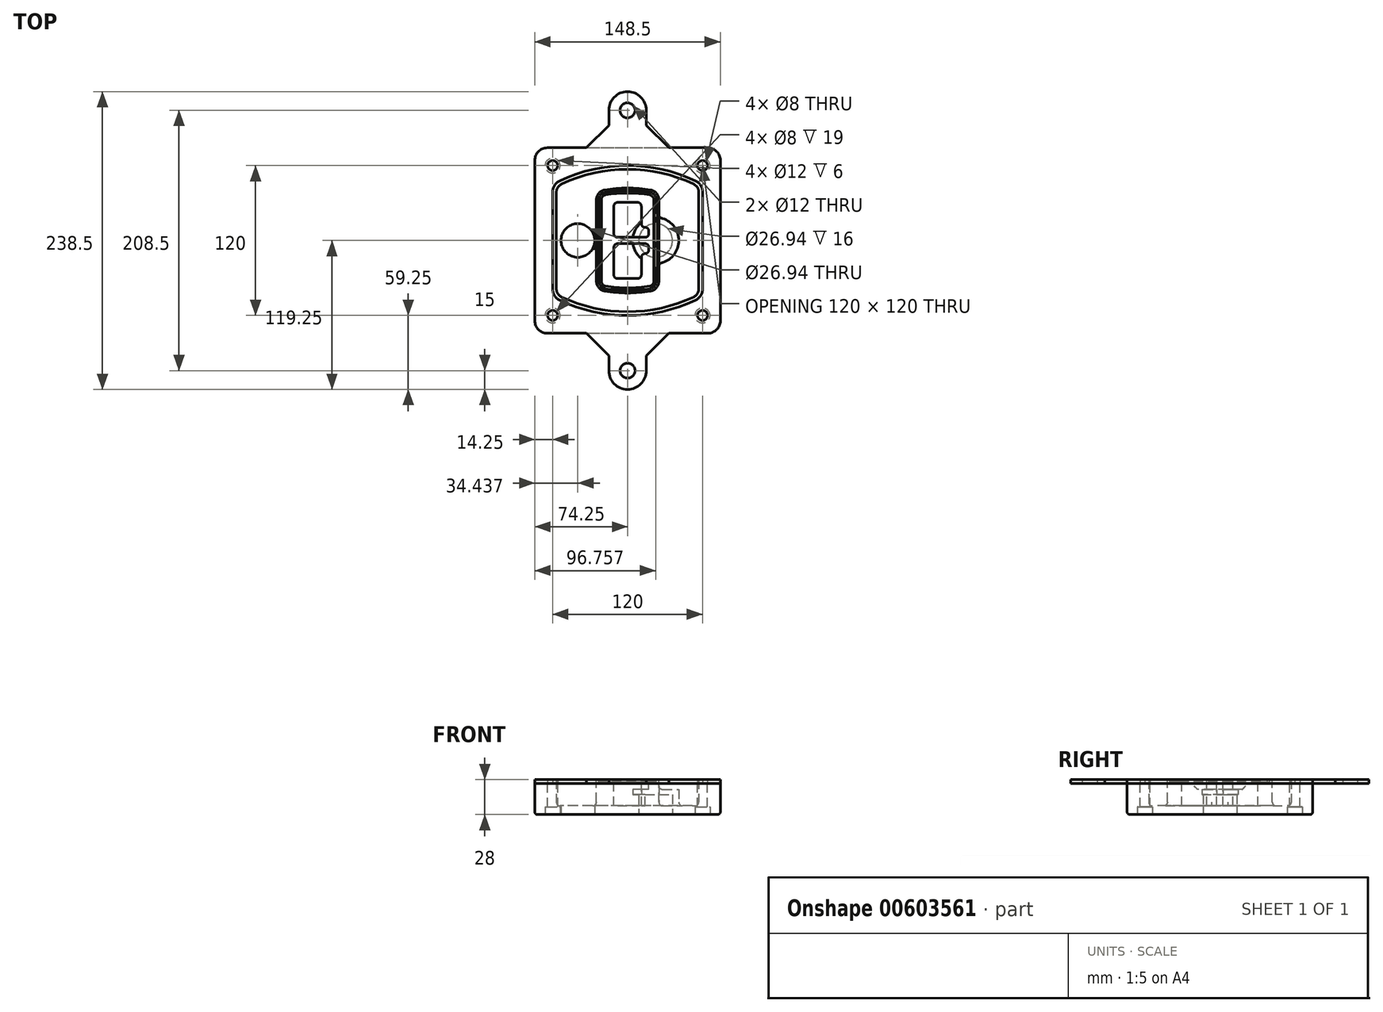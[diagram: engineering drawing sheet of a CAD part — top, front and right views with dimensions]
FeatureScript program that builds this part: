
annotation { "Feature Type Name" : "Feature", "Feature Type Description" : "" }
export const myFeature = defineFeature(function(context is Context, id is Id, definition is map)
    precondition{}
    {
        {
            var Q0;
            Q0=qCreatedBy(makeId("Top.planeOp"),FACE);
            var sketch = newSketch(context, id + "F0", { "sketchPlane" : qUnion([Q0])});
            skPoint(sketch, "E0.rect.middle", {"position": v(0, 0) * mm});
            skLineSegment(sketch, "E1.bottom", {"start": v(-64.25, -74.25) * mm, "end": v(64.25, -74.25) * mm});
            skLineSegment(sketch, "E1.top", {"start": v(-64.25, 74.25) * mm, "end": v(64.25, 74.25) * mm});
            skLineSegment(sketch, "E1.left", {"start": v(-74.25, -64.25) * mm, "end": v(-74.25, 64.25) * mm});
            skLineSegment(sketch, "E1.right", {"start": v(74.25, -64.25) * mm, "end": v(74.25, 64.25) * mm});
            skLineSegment(sketch, "E2", {"start": v(-74.25, 74.25) * mm, "end": v(74.25, -74.25) * mm, "construction": true});
            skLineSegment(sketch, "E3", {"start": v(74.25, 74.25) * mm, "end": v(-74.25, -74.25) * mm, "construction": true});
            skCircle(sketch, "E4", {"center": v(-60, 60) * mm, "radius": 4 * mm});
            skCircle(sketch, "E5", {"center": v(60, 60) * mm, "radius": 4 * mm});
            skCircle(sketch, "E6", {"center": v(60, -60) * mm, "radius": 4 * mm});
            skCircle(sketch, "E7", {"center": v(-60, -60) * mm, "radius": 4 * mm});
            skLineSegment(sketch, "E8", {"start": v(-60, 60) * mm, "end": v(60, 60) * mm, "construction": true});
            skLineSegment(sketch, "E9", {"start": v(60, 60) * mm, "end": v(60, -60) * mm, "construction": true});
            skLineSegment(sketch, "E10", {"start": v(60, -60) * mm, "end": v(-60, -60) * mm, "construction": true});
            skLineSegment(sketch, "E11", {"start": v(-60, -60) * mm, "end": v(-60, 60) * mm, "construction": true});
            skLineSegment(sketch, "E12", {"start": v(-60, 38.83) * mm, "end": v(-60, -38.83) * mm});
            skLineSegment(sketch, "E13", {"start": v(60, 38.83) * mm, "end": v(60, -38.83) * mm});
            skArc(sketch, "E14", {"start": v(54.26, 47.88) * mm, "mid": v(0, 60) * mm, "end": v(-54.26, 47.88) * mm});
            skArc(sketch, "E15", {"start": v(-54.26, -47.88) * mm, "mid": v(0, -60) * mm, "end": v(54.26, -47.88) * mm});
            skLineSegment(sketch, "E16", {"start": v(-60, 0) * mm, "end": v(60, 0) * mm, "construction": true});
            skPoint(sketch, "E17.visualSharp", {"position": v(-60, -45) * mm});
            skArc(sketch, "E17.filletArc", {"start": v(-60, -38.83) * mm, "mid": v(-58.44, -44.2) * mm, "end": v(-54.26, -47.88) * mm});
            skPoint(sketch, "E18.visualSharp", {"position": v(-60, 45) * mm});
            skArc(sketch, "E18.filletArc", {"start": v(-54.26, 47.88) * mm, "mid": v(-58.44, 44.2) * mm, "end": v(-60, 38.83) * mm});
            skPoint(sketch, "E19.visualSharp", {"position": v(60, 45) * mm});
            skArc(sketch, "E19.filletArc", {"start": v(60, 38.83) * mm, "mid": v(58.44, 44.2) * mm, "end": v(54.26, 47.88) * mm});
            skPoint(sketch, "E20.visualSharp", {"position": v(60, -45) * mm});
            skArc(sketch, "E20.filletArc", {"start": v(54.26, -47.88) * mm, "mid": v(58.44, -44.2) * mm, "end": v(60, -38.83) * mm});
            skPoint(sketch, "E21.visualSharp", {"position": v(-74.25, 74.25) * mm});
            skArc(sketch, "E21.filletArc", {"start": v(-64.25, 74.25) * mm, "mid": v(-71.32, 71.32) * mm, "end": v(-74.25, 64.25) * mm});
            skPoint(sketch, "E22.visualSharp", {"position": v(74.25, 74.25) * mm});
            skArc(sketch, "E22.filletArc", {"start": v(74.25, 64.25) * mm, "mid": v(71.32, 71.32) * mm, "end": v(64.25, 74.25) * mm});
            skPoint(sketch, "E23.visualSharp", {"position": v(74.25, -74.25) * mm});
            skArc(sketch, "E23.filletArc", {"start": v(64.25, -74.25) * mm, "mid": v(71.32, -71.32) * mm, "end": v(74.25, -64.25) * mm});
            skPoint(sketch, "E24.visualSharp", {"position": v(-74.25, -74.25) * mm});
            skArc(sketch, "E24.filletArc", {"start": v(-74.25, -64.25) * mm, "mid": v(-71.32, -71.32) * mm, "end": v(-64.25, -74.25) * mm});
            skArc(sketch, "E25.0", {"start": v(57, 38.83) * mm, "mid": v(55.9, 42.58) * mm, "end": v(52.98, 45.17) * mm});
            skLineSegment(sketch, "E25.1", {"start": v(57, 38.83) * mm, "end": v(57, -38.83) * mm});
            skArc(sketch, "E25.2", {"start": v(52.98, -45.17) * mm, "mid": v(55.9, -42.58) * mm, "end": v(57, -38.83) * mm});
            skArc(sketch, "E25.3", {"start": v(-52.98, -45.17) * mm, "mid": v(0, -57) * mm, "end": v(52.98, -45.17) * mm});
            skArc(sketch, "E25.4", {"start": v(-57, -38.83) * mm, "mid": v(-55.9, -42.58) * mm, "end": v(-52.98, -45.17) * mm});
            skArc(sketch, "E25.5", {"start": v(52.98, 45.17) * mm, "mid": v(0, 57) * mm, "end": v(-52.98, 45.17) * mm});
            skLineSegment(sketch, "E25.6", {"start": v(-57, 38.83) * mm, "end": v(-57, -38.83) * mm});
            skArc(sketch, "E25.7", {"start": v(-52.98, 45.17) * mm, "mid": v(-55.9, 42.58) * mm, "end": v(-57, 38.83) * mm});
            skArc(sketch, "E26.0", {"start": v(-55.96, 51.5) * mm, "mid": v(-61.82, 46.33) * mm, "end": v(-64, 38.83) * mm});
            skArc(sketch, "E26.1", {"start": v(55.96, 51.5) * mm, "mid": v(0, 64) * mm, "end": v(-55.96, 51.5) * mm});
            skArc(sketch, "E26.2", {"start": v(64, 38.83) * mm, "mid": v(61.82, 46.33) * mm, "end": v(55.96, 51.5) * mm});
            skLineSegment(sketch, "E26.3", {"start": v(64, 38.83) * mm, "end": v(64, -38.83) * mm});
            skArc(sketch, "E26.4", {"start": v(55.96, -51.5) * mm, "mid": v(61.82, -46.33) * mm, "end": v(64, -38.83) * mm});
            skLineSegment(sketch, "E26.5", {"start": v(-64, 38.83) * mm, "end": v(-64, -38.83) * mm});
            skArc(sketch, "E26.6", {"start": v(-55.96, -51.5) * mm, "mid": v(0, -64) * mm, "end": v(55.96, -51.5) * mm});
            skArc(sketch, "E26.7", {"start": v(-64, -38.83) * mm, "mid": v(-61.82, -46.33) * mm, "end": v(-55.96, -51.5) * mm});
            skSolve(sketch);
        }
        {
            var Q0;
            Q0=makeQuery(id+"F0.imprint","IMPRINT",FACE,{"disambiguationData":[TD([[makeQuery(id+"F0.imprint","IMPRINT",EDGE,{"derivedFrom":sQuery(id+"F0.wireOp",EDGE,"E1.bottom")}),1.0]])]});
            var Q1;
            Q1=makeQuery(id+"F0.imprint","IMPRINT",FACE,{"disambiguationData":[TD([[makeQuery(id+"F0.imprint","IMPRINT",EDGE,{"derivedFrom":sQuery(id+"F0.wireOp",EDGE,"E12")}),1.0]])]});
            var Q2;
            Q2=makeQuery(id+"F0.imprint","IMPRINT",FACE,{"disambiguationData":[TD([[makeQuery(id+"F0.imprint","IMPRINT",EDGE,{"derivedFrom":sQuery(id+"F0.wireOp",EDGE,"E25.0")}),1.0]])]});
            var Q3;
            Q3=makeQuery(id+"F0.imprint","IMPRINT",FACE,{"disambiguationData":[TD([[makeQuery(id+"F0.imprint","IMPRINT",EDGE,{"derivedFrom":sQuery(id+"F0.wireOp",EDGE,"E12")}),-1.0]])]});
            extrude(context, id + "F1", {"entities" : qUnion([Q0, Q1, Q2, Q3]), "oppositeDirection" : true, "depth" : 25 * mm});
        }
        {
            var Q0;
            Q0=makeQuery(id+"F0.imprint","IMPRINT",FACE,{"disambiguationData":[TD([[makeQuery(id+"F0.imprint","IMPRINT",EDGE,{"derivedFrom":sQuery(id+"F0.wireOp",EDGE,"E12")}),1.0]])]});
            extrude(context, id + "F2", {"entities" : qUnion([Q0]), "operationType" : NewBodyOperationType.ADD, "depth" : 3 * mm});
        }
        {
            var Q0;
            Q0=makeQuery(id+"F0.imprint","IMPRINT",FACE,{"disambiguationData":[TD([[makeQuery(id+"F0.imprint","IMPRINT",EDGE,{"derivedFrom":sQuery(id+"F0.wireOp",EDGE,"E25.0")}),1.0]])]});
            extrude(context, id + "F3", {"entities" : qUnion([Q0]), "operationType" : NewBodyOperationType.REMOVE, "oppositeDirection" : true, "depth" : 18 * mm});
        }
        {
            var Q0;
            Q0=makeQuery(id+"F2.opExtrude","CAP_FACE",FACE,{"disambiguationData":[OSD([sQuery(id+"F0.wireOp",EDGE,"E12"),sQuery(id+"F0.wireOp",EDGE,"E13"),sQuery(id+"F0.wireOp",EDGE,"E14"),sQuery(id+"F0.wireOp",EDGE,"E15"),sQuery(id+"F0.wireOp",EDGE,"E17.filletArc"),sQuery(id+"F0.wireOp",EDGE,"E18.filletArc"),sQuery(id+"F0.wireOp",EDGE,"E19.filletArc"),sQuery(id+"F0.wireOp",EDGE,"E20.filletArc"),sQuery(id+"F0.wireOp",EDGE,"E25.0"),sQuery(id+"F0.wireOp",EDGE,"E25.1"),sQuery(id+"F0.wireOp",EDGE,"E25.2"),sQuery(id+"F0.wireOp",EDGE,"E25.3"),sQuery(id+"F0.wireOp",EDGE,"E25.4"),sQuery(id+"F0.wireOp",EDGE,"E25.5"),sQuery(id+"F0.wireOp",EDGE,"E25.6"),sQuery(id+"F0.wireOp",EDGE,"E25.7")])],"isStart":false});
            var sketch = newSketch(context, id + "F4", { "sketchPlane" : qUnion([Q0])});
            skArc(sketch, "E27.0", {"start": v(-18.34, -40.45) * mm, "mid": v(0, -42) * mm, "end": v(18.34, -40.45) * mm});
            skArc(sketch, "E28.0", {"start": v(18.34, 40.45) * mm, "mid": v(0, 42) * mm, "end": v(-18.34, 40.45) * mm});
            skLineSegment(sketch, "E29", {"start": v(-25, 32.57) * mm, "end": v(-25, -32.57) * mm});
            skLineSegment(sketch, "E30", {"start": v(25, 32.57) * mm, "end": v(25, -32.57) * mm});
            skLineSegment(sketch, "E31", {"start": v(-25, 39.1) * mm, "end": v(25, 39.1) * mm, "construction": true});
            skLineSegment(sketch, "E32", {"start": v(-25, -39.1) * mm, "end": v(25, -39.1) * mm, "construction": true});
            skPoint(sketch, "E33.visualSharp", {"position": v(-25, 39.1) * mm});
            skArc(sketch, "E33.filletArc", {"start": v(-18.34, 40.45) * mm, "mid": v(-23.11, 37.73) * mm, "end": v(-25, 32.57) * mm});
            skPoint(sketch, "E34.visualSharp", {"position": v(25, 39.1) * mm});
            skArc(sketch, "E34.filletArc", {"start": v(25, 32.57) * mm, "mid": v(23.11, 37.73) * mm, "end": v(18.34, 40.45) * mm});
            skPoint(sketch, "E35.visualSharp", {"position": v(25, -39.1) * mm});
            skArc(sketch, "E35.filletArc", {"start": v(18.34, -40.45) * mm, "mid": v(23.11, -37.73) * mm, "end": v(25, -32.57) * mm});
            skPoint(sketch, "E36.visualSharp", {"position": v(-25, -39.1) * mm});
            skArc(sketch, "E36.filletArc", {"start": v(-25, -32.57) * mm, "mid": v(-23.11, -37.73) * mm, "end": v(-18.34, -40.45) * mm});
            skArc(sketch, "E37.0", {"start": v(52.98, 45.17) * mm, "mid": v(0, 57) * mm, "end": v(-52.98, 45.17) * mm});
            skArc(sketch, "E37.1", {"start": v(-52.98, 45.17) * mm, "mid": v(-55.9, 42.58) * mm, "end": v(-57, 38.83) * mm});
            skLineSegment(sketch, "E37.2", {"start": v(-57, 38.83) * mm, "end": v(-57, -38.83) * mm});
            skArc(sketch, "E37.3", {"start": v(-57, -38.83) * mm, "mid": v(-55.9, -42.58) * mm, "end": v(-52.98, -45.17) * mm});
            skArc(sketch, "E37.4", {"start": v(-52.98, -45.17) * mm, "mid": v(0, -57) * mm, "end": v(52.98, -45.17) * mm});
            skArc(sketch, "E37.5", {"start": v(52.98, -45.17) * mm, "mid": v(55.9, -42.58) * mm, "end": v(57, -38.83) * mm});
            skLineSegment(sketch, "E37.6", {"start": v(57, 38.83) * mm, "end": v(57, -38.83) * mm});
            skArc(sketch, "E37.7", {"start": v(57, 38.83) * mm, "mid": v(55.9, 42.58) * mm, "end": v(52.98, 45.17) * mm});
            skLineSegment(sketch, "E38.0", {"start": v(23, 32.57) * mm, "end": v(23, -32.57) * mm});
            skArc(sketch, "E38.1", {"start": v(18, -38.48) * mm, "mid": v(21.58, -36.44) * mm, "end": v(23, -32.57) * mm});
            skArc(sketch, "E38.2", {"start": v(-18, -38.48) * mm, "mid": v(0, -40) * mm, "end": v(18, -38.48) * mm});
            skArc(sketch, "E38.3", {"start": v(-23, -32.57) * mm, "mid": v(-21.58, -36.44) * mm, "end": v(-18, -38.48) * mm});
            skLineSegment(sketch, "E38.4", {"start": v(-23, 32.57) * mm, "end": v(-23, -32.57) * mm});
            skArc(sketch, "E38.5", {"start": v(23, 32.57) * mm, "mid": v(21.58, 36.44) * mm, "end": v(18, 38.48) * mm});
            skArc(sketch, "E38.6", {"start": v(-18, 38.48) * mm, "mid": v(-21.58, 36.44) * mm, "end": v(-23, 32.57) * mm});
            skArc(sketch, "E38.7", {"start": v(18, 38.48) * mm, "mid": v(0, 40) * mm, "end": v(-18, 38.48) * mm});
            skArc(sketch, "E39.0", {"start": v(21, 32.57) * mm, "mid": v(20.06, 35.15) * mm, "end": v(17.67, 36.5) * mm});
            skLineSegment(sketch, "E39.1", {"start": v(21, 32.57) * mm, "end": v(21, -32.57) * mm});
            skArc(sketch, "E39.2", {"start": v(17.67, -36.5) * mm, "mid": v(20.06, -35.15) * mm, "end": v(21, -32.57) * mm});
            skArc(sketch, "E39.3", {"start": v(-17.67, -36.5) * mm, "mid": v(0, -38) * mm, "end": v(17.67, -36.5) * mm});
            skArc(sketch, "E39.4", {"start": v(-21, -32.57) * mm, "mid": v(-20.06, -35.15) * mm, "end": v(-17.67, -36.5) * mm});
            skArc(sketch, "E39.5", {"start": v(17.67, 36.5) * mm, "mid": v(0, 38) * mm, "end": v(-17.67, 36.5) * mm});
            skLineSegment(sketch, "E39.6", {"start": v(-21, 32.57) * mm, "end": v(-21, -32.57) * mm});
            skArc(sketch, "E39.7", {"start": v(-17.67, 36.5) * mm, "mid": v(-20.06, 35.15) * mm, "end": v(-21, 32.57) * mm});
            skLineSegment(sketch, "E40", {"start": v(-25, 0) * mm, "end": v(25, 0) * mm, "construction": true});
            skLineSegment(sketch, "E41", {"start": v(-11, 5.5) * mm, "end": v(-11, 27.5) * mm});
            skLineSegment(sketch, "E42", {"start": v(-8, 30.5) * mm, "end": v(8, 30.5) * mm});
            skLineSegment(sketch, "E43", {"start": v(11, 27.5) * mm, "end": v(11, 13.5) * mm});
            skLineSegment(sketch, "E44", {"start": v(14, 10.5) * mm, "end": v(14, 10.5) * mm});
            skLineSegment(sketch, "E45", {"start": v(17, 7.5) * mm, "end": v(17, 5.5) * mm});
            skLineSegment(sketch, "E46", {"start": v(14, 2.5) * mm, "end": v(-8, 2.5) * mm});
            skPoint(sketch, "E47.visualSharp", {"position": v(-11, 30.5) * mm});
            skArc(sketch, "E47.filletArc", {"start": v(-8, 30.5) * mm, "mid": v(-10.12, 29.62) * mm, "end": v(-11, 27.5) * mm});
            skPoint(sketch, "E48.visualSharp", {"position": v(11, 30.5) * mm});
            skArc(sketch, "E48.filletArc", {"start": v(11, 27.5) * mm, "mid": v(10.12, 29.62) * mm, "end": v(8, 30.5) * mm});
            skPoint(sketch, "E49.visualSharp", {"position": v(11, 10.5) * mm});
            skArc(sketch, "E49.filletArc", {"start": v(11, 13.5) * mm, "mid": v(11.88, 11.38) * mm, "end": v(14, 10.5) * mm});
            skPoint(sketch, "E50.visualSharp", {"position": v(17, 10.5) * mm});
            skArc(sketch, "E50.filletArc", {"start": v(17, 7.5) * mm, "mid": v(16.12, 9.62) * mm, "end": v(14, 10.5) * mm});
            skPoint(sketch, "E51.visualSharp", {"position": v(17, 2.5) * mm});
            skArc(sketch, "E51.filletArc", {"start": v(14, 2.5) * mm, "mid": v(16.12, 3.38) * mm, "end": v(17, 5.5) * mm});
            skPoint(sketch, "E52.visualSharp", {"position": v(-11, 2.5) * mm});
            skArc(sketch, "E52.filletArc", {"start": v(-11, 5.5) * mm, "mid": v(-10.12, 3.38) * mm, "end": v(-8, 2.5) * mm});
            skLineSegment(sketch, "E53.0.MirrorCS", {"start": v(14, -2.5) * mm, "end": v(-8, -2.5) * mm});
            skArc(sketch, "E54.0.MirrorCS", {"start": v(-11, -5.5) * mm, "mid": v(-10.12, -3.38) * mm, "end": v(-8, -2.5) * mm});
            skLineSegment(sketch, "E55.0.MirrorCS", {"start": v(-11, -5.5) * mm, "end": v(-11, -27.5) * mm});
            skArc(sketch, "E56.0.MirrorCS", {"start": v(-8, -30.5) * mm, "mid": v(-10.12, -29.62) * mm, "end": v(-11, -27.5) * mm});
            skLineSegment(sketch, "E57.0.MirrorCS", {"start": v(-8, -30.5) * mm, "end": v(8, -30.5) * mm});
            skArc(sketch, "E58.0.MirrorCS", {"start": v(11, -27.5) * mm, "mid": v(10.12, -29.62) * mm, "end": v(8, -30.5) * mm});
            skLineSegment(sketch, "E59.0.MirrorCS", {"start": v(11, -27.5) * mm, "end": v(11, -13.5) * mm});
            skArc(sketch, "E60.0.MirrorCS", {"start": v(11, -13.5) * mm, "mid": v(11.88, -11.38) * mm, "end": v(14, -10.5) * mm});
            skArc(sketch, "E61.0.MirrorCS", {"start": v(17, -7.5) * mm, "mid": v(16.12, -9.62) * mm, "end": v(14, -10.5) * mm});
            skLineSegment(sketch, "E62.0.MirrorCS", {"start": v(17, -7.5) * mm, "end": v(17, -5.5) * mm});
            skArc(sketch, "E63.0.MirrorCS", {"start": v(14, -2.5) * mm, "mid": v(16.12, -3.38) * mm, "end": v(17, -5.5) * mm});
            skSolve(sketch);
        }
        {
            var Q0;
            Q0=makeQuery(id+"F4.imprint","IMPRINT",FACE,{"disambiguationData":[TD([[makeQuery(id+"F4.imprint","IMPRINT",EDGE,{"derivedFrom":sQuery(id+"F4.wireOp",EDGE,"E27.0")}),1.0]])]});
            var Q1;
            Q1=makeQuery(id+"F4.imprint","IMPRINT",FACE,{"disambiguationData":[TD([[makeQuery(id+"F4.imprint","IMPRINT",EDGE,{"derivedFrom":sQuery(id+"F4.wireOp",EDGE,"E38.0")}),-1.0]])]});
            var Q2;
            Q2=makeQuery(id+"F4.imprint","IMPRINT",FACE,{"disambiguationData":[TD([[makeQuery(id+"F4.imprint","IMPRINT",EDGE,{"derivedFrom":sQuery(id+"F4.wireOp",EDGE,"E39.0")}),1.0]])]});
            extrude(context, id + "F5", {"entities" : qUnion([Q0, Q1, Q2]), "operationType" : NewBodyOperationType.ADD, "endBound" : BoundingType.UP_TO_NEXT, "oppositeDirection" : true, "depth" : 25 * mm});
        }
        {
            var Q0;
            Q0=makeQuery(id+"F4.imprint","IMPRINT",FACE,{"disambiguationData":[TD([[makeQuery(id+"F4.imprint","IMPRINT",EDGE,{"derivedFrom":sQuery(id+"F4.wireOp",EDGE,"E38.0")}),-1.0]])]});
            extrude(context, id + "F6", {"entities" : qUnion([Q0]), "operationType" : NewBodyOperationType.REMOVE, "oppositeDirection" : true, "depth" : 2 * mm});
        }
        {
            var Q0;
            Q0=makeQuery(id+"F1.opExtrude","CAP_FACE",FACE,{"disambiguationData":[OSD([sQuery(id+"F0.wireOp",EDGE,"E1.bottom"),sQuery(id+"F0.wireOp",EDGE,"E1.top"),sQuery(id+"F0.wireOp",EDGE,"E1.left"),sQuery(id+"F0.wireOp",EDGE,"E1.right"),sQuery(id+"F0.wireOp",EDGE,"E4"),sQuery(id+"F0.wireOp",EDGE,"E5"),sQuery(id+"F0.wireOp",EDGE,"E6"),sQuery(id+"F0.wireOp",EDGE,"E7"),sQuery(id+"F0.wireOp",EDGE,"E21.filletArc"),sQuery(id+"F0.wireOp",EDGE,"E22.filletArc"),sQuery(id+"F0.wireOp",EDGE,"E23.filletArc"),sQuery(id+"F0.wireOp",EDGE,"E24.filletArc")])],"isStart":false});
            var sketch = newSketch(context, id + "F7", { "sketchPlane" : qUnion([Q0])});
            skCircle(sketch, "E64", {"center": v(22.5, 0) * mm, "radius": 13.47 * mm});
            skCircle(sketch, "E65", {"center": v(-39.81, 0) * mm, "radius": 13.47 * mm});
            skLineSegment(sketch, "E66", {"start": v(74.25, 0) * mm, "end": v(-74.25, 0) * mm});
            skCircle(sketch, "E67", {"center": v(22.5, 0) * mm, "radius": 18.47 * mm});
            skCircle(sketch, "E68", {"center": v(60, -60) * mm, "radius": 6 * mm});
            skCircle(sketch, "E69", {"center": v(-60, -60) * mm, "radius": 6 * mm});
            skCircle(sketch, "E70", {"center": v(-60, 60) * mm, "radius": 6 * mm});
            skCircle(sketch, "E71", {"center": v(60, 60) * mm, "radius": 6 * mm});
            skSolve(sketch);
        }
        {
            var Q0;
            {var subQ1=sQuery(id+"F7.wireOp",EDGE,"E66");var subQ4=sQuery(id+"F7.wireOp",EDGE,"E64");var subQ6=makeQuery(id+"F7.imprint","INTERSECT",VERTEX,{"disambiguationData":[OD(0.0)],"derivedFrom":[subQ4,subQ1]});Q0=makeQuery(id+"F7.imprint","IMPRINT",FACE,{"disambiguationData":[TD([[makeQuery(id+"F7.imprint","IMPRINT",EDGE,{"disambiguationData":[TD([[subQ6,-1.0]])],"derivedFrom":subQ4}),-1.0]])]});}
            var Q1;
            {var subQ0=sQuery(id+"F7.wireOp",EDGE,"E66");var subQ1=sQuery(id+"F7.wireOp",EDGE,"E64");var subQ3=makeQuery(id+"F7.imprint","INTERSECT",VERTEX,{"disambiguationData":[OD(0.0)],"derivedFrom":[subQ1,subQ0]});Q1=makeQuery(id+"F7.imprint","IMPRINT",FACE,{"disambiguationData":[TD([[makeQuery(id+"F7.imprint","IMPRINT",EDGE,{"disambiguationData":[TD([[subQ3,-1.0]])],"derivedFrom":subQ1}),1.0]])]});}
            var Q2;
            {var subQ0=sQuery(id+"F7.wireOp",EDGE,"E66");var subQ1=sQuery(id+"F7.wireOp",EDGE,"E64");var subQ3=makeQuery(id+"F7.imprint","INTERSECT",VERTEX,{"disambiguationData":[OD(0.0)],"derivedFrom":[subQ1,subQ0]});Q2=makeQuery(id+"F7.imprint","IMPRINT",FACE,{"disambiguationData":[TD([[makeQuery(id+"F7.imprint","IMPRINT",EDGE,{"disambiguationData":[TD([[subQ3,1.0]])],"derivedFrom":subQ1}),1.0]])]});}
            var Q3;
            {var subQ1=sQuery(id+"F7.wireOp",EDGE,"E66");var subQ4=sQuery(id+"F7.wireOp",EDGE,"E64");var subQ6=makeQuery(id+"F7.imprint","INTERSECT",VERTEX,{"disambiguationData":[OD(0.0)],"derivedFrom":[subQ4,subQ1]});Q3=makeQuery(id+"F7.imprint","IMPRINT",FACE,{"disambiguationData":[TD([[makeQuery(id+"F7.imprint","IMPRINT",EDGE,{"disambiguationData":[TD([[subQ6,1.0]])],"derivedFrom":subQ4}),-1.0]])]});}
            extrude(context, id + "F8", {"entities" : qUnion([Q0, Q1, Q2, Q3]), "operationType" : NewBodyOperationType.ADD, "oppositeDirection" : true, "depth" : 20 * mm});
        }
        {
            var Q0;
            {var subQ0=sQuery(id+"F7.wireOp",EDGE,"E66");var subQ1=sQuery(id+"F7.wireOp",EDGE,"E64");var subQ3=makeQuery(id+"F7.imprint","INTERSECT",VERTEX,{"disambiguationData":[OD(0.0)],"derivedFrom":[subQ1,subQ0]});Q0=makeQuery(id+"F7.imprint","IMPRINT",FACE,{"disambiguationData":[TD([[makeQuery(id+"F7.imprint","IMPRINT",EDGE,{"disambiguationData":[TD([[subQ3,-1.0]])],"derivedFrom":subQ1}),1.0]])]});}
            var Q1;
            {var subQ0=sQuery(id+"F7.wireOp",EDGE,"E66");var subQ1=sQuery(id+"F7.wireOp",EDGE,"E64");var subQ3=makeQuery(id+"F7.imprint","INTERSECT",VERTEX,{"disambiguationData":[OD(0.0)],"derivedFrom":[subQ1,subQ0]});Q1=makeQuery(id+"F7.imprint","IMPRINT",FACE,{"disambiguationData":[TD([[makeQuery(id+"F7.imprint","IMPRINT",EDGE,{"disambiguationData":[TD([[subQ3,1.0]])],"derivedFrom":subQ1}),1.0]])]});}
            extrude(context, id + "F9", {"entities" : qUnion([Q0, Q1]), "operationType" : NewBodyOperationType.REMOVE, "oppositeDirection" : true, "depth" : 16 * mm});
        }
        {
            var Q0;
            {var subQ0=sQuery(id+"F7.wireOp",EDGE,"E66");var subQ1=sQuery(id+"F7.wireOp",EDGE,"E65");var subQ3=makeQuery(id+"F7.imprint","INTERSECT",VERTEX,{"disambiguationData":[OD(0.0)],"derivedFrom":[subQ1,subQ0]});Q0=makeQuery(id+"F7.imprint","IMPRINT",FACE,{"disambiguationData":[TD([[makeQuery(id+"F7.imprint","IMPRINT",EDGE,{"disambiguationData":[TD([[subQ3,-1.0]])],"derivedFrom":subQ1}),1.0]])]});}
            var Q1;
            {var subQ0=sQuery(id+"F7.wireOp",EDGE,"E66");var subQ1=sQuery(id+"F7.wireOp",EDGE,"E65");var subQ3=makeQuery(id+"F7.imprint","INTERSECT",VERTEX,{"disambiguationData":[OD(0.0)],"derivedFrom":[subQ1,subQ0]});Q1=makeQuery(id+"F7.imprint","IMPRINT",FACE,{"disambiguationData":[TD([[makeQuery(id+"F7.imprint","IMPRINT",EDGE,{"disambiguationData":[TD([[subQ3,1.0]])],"derivedFrom":subQ1}),1.0]])]});}
            extrude(context, id + "F10", {"entities" : qUnion([Q0, Q1]), "operationType" : NewBodyOperationType.REMOVE, "oppositeDirection" : true, "depth" : 25 * mm});
        }
        {
            var Q0;
            Q0=makeQuery(id+"F7.imprint","IMPRINT",FACE,{"disambiguationData":[TD([[makeQuery(id+"F7.imprint","IMPRINT",EDGE,{"derivedFrom":sQuery(id+"F7.wireOp",EDGE,"E68")}),1.0]])]});
            var Q1;
            Q1=makeQuery(id+"F7.imprint","IMPRINT",FACE,{"disambiguationData":[TD([[makeQuery(id+"F7.imprint","IMPRINT",EDGE,{"derivedFrom":makeQuery(id+"F1.opExtrude","CAP_EDGE",EDGE,{"disambiguationData":[OSD([sQuery(id+"F0.wireOp",EDGE,"E5")])],"isStart":false})}),-1.0]])]});
            var Q2;
            Q2=makeQuery(id+"F7.imprint","IMPRINT",FACE,{"disambiguationData":[TD([[makeQuery(id+"F7.imprint","IMPRINT",EDGE,{"derivedFrom":sQuery(id+"F7.wireOp",EDGE,"E69")}),1.0]])]});
            var Q3;
            Q3=makeQuery(id+"F7.imprint","IMPRINT",FACE,{"disambiguationData":[TD([[makeQuery(id+"F7.imprint","IMPRINT",EDGE,{"derivedFrom":makeQuery(id+"F1.opExtrude","CAP_EDGE",EDGE,{"disambiguationData":[OSD([sQuery(id+"F0.wireOp",EDGE,"E4")])],"isStart":false})}),-1.0]])]});
            var Q4;
            Q4=makeQuery(id+"F7.imprint","IMPRINT",FACE,{"disambiguationData":[TD([[makeQuery(id+"F7.imprint","IMPRINT",EDGE,{"derivedFrom":sQuery(id+"F7.wireOp",EDGE,"E70")}),1.0]])]});
            var Q5;
            Q5=makeQuery(id+"F7.imprint","IMPRINT",FACE,{"disambiguationData":[TD([[makeQuery(id+"F7.imprint","IMPRINT",EDGE,{"derivedFrom":makeQuery(id+"F1.opExtrude","CAP_EDGE",EDGE,{"disambiguationData":[OSD([sQuery(id+"F0.wireOp",EDGE,"E7")])],"isStart":false})}),-1.0]])]});
            var Q6;
            Q6=makeQuery(id+"F7.imprint","IMPRINT",FACE,{"disambiguationData":[TD([[makeQuery(id+"F7.imprint","IMPRINT",EDGE,{"derivedFrom":sQuery(id+"F7.wireOp",EDGE,"E71")}),1.0]])]});
            var Q7;
            Q7=makeQuery(id+"F7.imprint","IMPRINT",FACE,{"disambiguationData":[TD([[makeQuery(id+"F7.imprint","IMPRINT",EDGE,{"derivedFrom":makeQuery(id+"F1.opExtrude","CAP_EDGE",EDGE,{"disambiguationData":[OSD([sQuery(id+"F0.wireOp",EDGE,"E6")])],"isStart":false})}),-1.0]])]});
            extrude(context, id + "F11", {"entities" : qUnion([Q0, Q1, Q2, Q3, Q4, Q5, Q6, Q7]), "operationType" : NewBodyOperationType.REMOVE, "oppositeDirection" : true, "depth" : 6 * mm});
        }
        {
            var Q0;
            Q0=makeQuery(id+"F9.boolean.opBoolean","COPY",FACE,{"derivedFrom":makeQuery(id+"F9.opExtrude","CAP_FACE",FACE,{"disambiguationData":[OSD([sQuery(id+"F7.wireOp",EDGE,"E64")])],"isStart":false})});
            var sketch = newSketch(context, id + "F12", { "sketchPlane" : qUnion([Q0])});
            skArc(sketch, "E72.0", {"start": v(11, 14.45) * mm, "mid": v(6.45, 9.13) * mm, "end": v(4.2, 2.5) * mm});
            skArc(sketch, "E72.1", {"start": v(4.2, -2.5) * mm, "mid": v(6.45, -9.13) * mm, "end": v(11, -14.45) * mm});
            skLineSegment(sketch, "E73", {"start": v(4.2, -2.5) * mm, "end": v(14, -2.5) * mm});
            skLineSegment(sketch, "E74.0", {"start": v(14, 2.5) * mm, "end": v(4.2, 2.5) * mm});
            skArc(sketch, "E74.1", {"start": v(14, 2.5) * mm, "mid": v(16.12, 3.38) * mm, "end": v(17, 5.5) * mm});
            skLineSegment(sketch, "E74.2", {"start": v(17, 7.5) * mm, "end": v(17, 5.5) * mm});
            skArc(sketch, "E74.3", {"start": v(17, 7.5) * mm, "mid": v(16.12, 9.62) * mm, "end": v(14, 10.5) * mm});
            skArc(sketch, "E74.4", {"start": v(11, 13.5) * mm, "mid": v(11.88, 11.38) * mm, "end": v(14, 10.5) * mm});
            skLineSegment(sketch, "E74.5", {"start": v(11, 14.45) * mm, "end": v(11, 13.5) * mm});
            skLineSegment(sketch, "E74.7", {"start": v(14, -2.5) * mm, "end": v(4.2, -2.5) * mm});
            skArc(sketch, "E74.8", {"start": v(14, -2.5) * mm, "mid": v(16.12, -3.38) * mm, "end": v(17, -5.5) * mm});
            skLineSegment(sketch, "E74.9", {"start": v(17, -7.5) * mm, "end": v(17, -5.5) * mm});
            skArc(sketch, "E74.10", {"start": v(17, -7.5) * mm, "mid": v(16.12, -9.62) * mm, "end": v(14, -10.5) * mm});
            skArc(sketch, "E74.11", {"start": v(11, -13.5) * mm, "mid": v(11.88, -11.38) * mm, "end": v(14, -10.5) * mm});
            skLineSegment(sketch, "E74.12", {"start": v(11, -14.45) * mm, "end": v(11, -13.5) * mm});
            skPoint(sketch, "E75.orphan", {"position": v(11, -27.5) * mm});
            skPoint(sketch, "E76.orphan", {"position": v(-8, -2.5) * mm});
            skPoint(sketch, "E77.orphan", {"position": v(-8, 2.5) * mm});
            skPoint(sketch, "E78.orphan", {"position": v(11, 27.5) * mm});
            skSolve(sketch);
        }
        {
            var Q0;
            {var subQ7=sQuery(id+"F12.wireOp",EDGE,"E72.0");var subQ14=sQuery(id+"F12.wireOp",EDGE,"E72.1");var subQ16=sQuery(id+"F12.wireOp",EDGE,"E74.1");var subQ18=sQuery(id+"F12.wireOp",EDGE,"E74.8");Q0=qUnion([makeQuery(id+"F12.imprint","IMPRINT",FACE,{"disambiguationData":[TD([[makeQuery(id+"F12.imprint","IMPRINT",EDGE,{"derivedFrom":subQ7}),1.0]])]}),makeQuery(id+"F12.imprint","IMPRINT",FACE,{"disambiguationData":[TD([[makeQuery(id+"F12.imprint","IMPRINT",EDGE,{"derivedFrom":subQ14}),1.0]])]}),makeQuery(id+"F12.imprint","IMPRINT",FACE,{"disambiguationData":[TD([[makeQuery(id+"F12.imprint","IMPRINT",EDGE,{"derivedFrom":subQ16}),1.0]])]}),makeQuery(id+"F12.imprint","IMPRINT",FACE,{"disambiguationData":[TD([[makeQuery(id+"F12.imprint","IMPRINT",EDGE,{"derivedFrom":subQ18}),-1.0]])]})]);}
            var Q1;
            Q1=makeQuery(id+"F5.boolean.opBoolean","SPLIT",FACE,{"disambiguationData":[TD([makeQuery(id+"F5.opExtrude","SWEPT_FACE",FACE,{"disambiguationData":[OSD([sQuery(id+"F4.wireOp",EDGE,"E41")])]})])],"derivedFrom":makeQuery(id+"F3.boolean.opBoolean","COPY",FACE,{"derivedFrom":makeQuery(id+"F3.opExtrude","CAP_FACE",FACE,{"disambiguationData":[OSD([sQuery(id+"F0.wireOp",EDGE,"E25.0"),sQuery(id+"F0.wireOp",EDGE,"E25.1"),sQuery(id+"F0.wireOp",EDGE,"E25.2"),sQuery(id+"F0.wireOp",EDGE,"E25.3"),sQuery(id+"F0.wireOp",EDGE,"E25.4"),sQuery(id+"F0.wireOp",EDGE,"E25.5"),sQuery(id+"F0.wireOp",EDGE,"E25.6"),sQuery(id+"F0.wireOp",EDGE,"E25.7")])],"isStart":false})})});
            extrude(context, id + "F13", {"entities" : qUnion([Q0]), "operationType" : NewBodyOperationType.REMOVE, "endBound" : BoundingType.UP_TO_SURFACE, "endBoundEntityFace" : qUnion([Q1]), "depth" : 25 * mm});
        }
        {
            var Q0;
            Q0=makeQuery(id+"F3.boolean.opBoolean","COPY",EDGE,{"derivedFrom":makeQuery(id+"F3.opExtrude","CAP_EDGE",EDGE,{"disambiguationData":[OSD([sQuery(id+"F0.wireOp",EDGE,"E25.6")])],"isStart":false})});
            var Q1;
            Q1=makeQuery(id+"F8.boolean.opBoolean","INTERSECT",EDGE,{"derivedFrom":[makeQuery(id+"F5.opExtrude","SWEPT_FACE",FACE,{"disambiguationData":[OSD([sQuery(id+"F4.wireOp",EDGE,"E30")])]}),makeQuery(id+"F8.opExtrude","CAP_FACE",FACE,{"disambiguationData":[OSD([sQuery(id+"F7.wireOp",EDGE,"E67")])],"isStart":false})]});
            var Q2;
            Q2=makeQuery(id+"F8.boolean.opBoolean","INTERSECT",EDGE,{"disambiguationData":[OD(1.0)],"derivedFrom":[makeQuery(id+"F5.opExtrude","SWEPT_FACE",FACE,{"disambiguationData":[OSD([sQuery(id+"F4.wireOp",EDGE,"E30")])]}),makeQuery(id+"F8.opExtrude","SWEPT_FACE",FACE,{"disambiguationData":[OSD([sQuery(id+"F7.wireOp",EDGE,"E67")])]})]});
            var Q3;
            {var subQ0=sQuery(id+"F4.wireOp",EDGE,"E30");Q3=makeQuery(id+"F8.boolean.opBoolean","SPLIT",EDGE,{"disambiguationData":[TD([makeQuery(id+"F5.opExtrude","SWEPT_FACE",FACE,{"disambiguationData":[OSD([sQuery(id+"F4.wireOp",EDGE,"E35.filletArc")])]})])],"derivedFrom":makeQuery(id+"F5.opExtrude","CAP_EDGE",EDGE,{"disambiguationData":[OSD([subQ0])],"isStart":false})});}
            var Q4;
            {var subQ0=sQuery(id+"F0.wireOp",EDGE,"E25.7");var subQ1=sQuery(id+"F0.wireOp",EDGE,"E25.1");var subQ2=sQuery(id+"F0.wireOp",EDGE,"E25.6");var subQ3=sQuery(id+"F0.wireOp",EDGE,"E25.5");var subQ4=sQuery(id+"F0.wireOp",EDGE,"E25.4");var subQ5=sQuery(id+"F0.wireOp",EDGE,"E25.0");var subQ6=sQuery(id+"F0.wireOp",EDGE,"E25.2");var subQ7=sQuery(id+"F0.wireOp",EDGE,"E25.3");Q4=makeQuery(id+"F8.boolean.opBoolean","INTERSECT",EDGE,{"derivedFrom":[makeQuery(id+"F5.boolean.opBoolean","SPLIT",FACE,{"disambiguationData":[TD([makeQuery(id+"F2.opExtrude","SWEPT_FACE",FACE,{"disambiguationData":[OSD([subQ5])]})])],"derivedFrom":makeQuery(id+"F3.boolean.opBoolean","COPY",FACE,{"derivedFrom":makeQuery(id+"F3.opExtrude","CAP_FACE",FACE,{"disambiguationData":[OSD([subQ5,subQ1,subQ6,subQ7,subQ4,subQ3,subQ2,subQ0])],"isStart":false})})}),makeQuery(id+"F8.opExtrude","SWEPT_FACE",FACE,{"disambiguationData":[OSD([sQuery(id+"F7.wireOp",EDGE,"E67")])]})]});}
            var Q5;
            Q5=makeQuery(id+"F8.boolean.opBoolean","INTERSECT",EDGE,{"disambiguationData":[OD(0.0)],"derivedFrom":[makeQuery(id+"F5.opExtrude","SWEPT_FACE",FACE,{"disambiguationData":[OSD([sQuery(id+"F4.wireOp",EDGE,"E30")])]}),makeQuery(id+"F8.opExtrude","SWEPT_FACE",FACE,{"disambiguationData":[OSD([sQuery(id+"F7.wireOp",EDGE,"E67")])]})]});
            fillet(context, id + "F14", {"entities" : qUnion([Q0, Q1, Q2, Q3, Q4, Q5]), "radius" : 3 * mm, "tangentPropagation" : true, "allowEdgeOverflow" : false});
        }
        {
            var Q0;
            Q0=makeQuery(id+"F1.opExtrude","CAP_EDGE",EDGE,{"disambiguationData":[OSD([sQuery(id+"F0.wireOp",EDGE,"E1.bottom")])],"isStart":false});
            fillet(context, id + "F15", {"entities" : qUnion([Q0]), "radius" : 2 * mm, "tangentPropagation" : true, "allowEdgeOverflow" : false});
        }
        {
            var Q0;
            {var subQ0=sQuery(id+"F0.wireOp",EDGE,"E21.filletArc");var subQ1=sQuery(id+"F0.wireOp",EDGE,"E7");var subQ2=sQuery(id+"F0.wireOp",EDGE,"E6");var subQ3=sQuery(id+"F0.wireOp",EDGE,"E5");var subQ4=sQuery(id+"F0.wireOp",EDGE,"E4");var subQ5=sQuery(id+"F0.wireOp",EDGE,"E22.filletArc");var subQ6=sQuery(id+"F0.wireOp",EDGE,"E1.bottom");var subQ7=sQuery(id+"F0.wireOp",EDGE,"E1.right");var subQ8=sQuery(id+"F0.wireOp",EDGE,"E1.top");var subQ9=sQuery(id+"F0.wireOp",EDGE,"E1.left");var subQ10=sQuery(id+"F0.wireOp",EDGE,"E23.filletArc");var subQ11=sQuery(id+"F0.wireOp",EDGE,"E24.filletArc");Q0=makeQuery(id+"F2.boolean.opBoolean","SPLIT",FACE,{"disambiguationData":[TD([makeQuery(id+"F1.opExtrude","SWEPT_FACE",FACE,{"disambiguationData":[OSD([subQ6])]})])],"derivedFrom":makeQuery(id+"F1.opExtrude","CAP_FACE",FACE,{"disambiguationData":[OSD([subQ6,subQ8,subQ9,subQ7,subQ4,subQ3,subQ2,subQ1,subQ0,subQ5,subQ10,subQ11])],"isStart":true})});}
            var sketch = newSketch(context, id + "F16", { "sketchPlane" : qUnion([Q0])});
            skLineSegment(sketch, "E79.0", {"start": v(-64.25, 74.25) * mm, "end": v(64.25, 74.25) * mm});
            skArc(sketch, "E80.0", {"start": v(-64.25, 74.25) * mm, "mid": v(-71.32, 71.32) * mm, "end": v(-74.25, 64.25) * mm});
            skLineSegment(sketch, "E81.0", {"start": v(-74.25, -64.25) * mm, "end": v(-74.25, 64.25) * mm});
            skArc(sketch, "E82.0", {"start": v(-74.25, -64.25) * mm, "mid": v(-71.32, -71.32) * mm, "end": v(-64.25, -74.25) * mm});
            skLineSegment(sketch, "E83.0", {"start": v(-64.25, -74.25) * mm, "end": v(64.25, -74.25) * mm});
            skArc(sketch, "E84.0", {"start": v(64.25, -74.25) * mm, "mid": v(71.32, -71.32) * mm, "end": v(74.25, -64.25) * mm});
            skLineSegment(sketch, "E85.0", {"start": v(74.25, -64.25) * mm, "end": v(74.25, 64.25) * mm});
            skArc(sketch, "E86.0", {"start": v(74.25, 64.25) * mm, "mid": v(71.32, 71.32) * mm, "end": v(64.25, 74.25) * mm});
            skCircle(sketch, "E87.0", {"center": v(60, 60) * mm, "radius": 4 * mm});
            skCircle(sketch, "E88.0", {"center": v(-60, 60) * mm, "radius": 4 * mm});
            skCircle(sketch, "E89.0", {"center": v(-60, -60) * mm, "radius": 4 * mm});
            skCircle(sketch, "E90.0", {"center": v(60, -60) * mm, "radius": 4 * mm});
            skArc(sketch, "E91.0", {"start": v(-54.26, -47.88) * mm, "mid": v(0, -60) * mm, "end": v(54.26, -47.88) * mm});
            skArc(sketch, "E92.0", {"start": v(-60, -38.83) * mm, "mid": v(-58.44, -44.2) * mm, "end": v(-54.26, -47.88) * mm});
            skLineSegment(sketch, "E93.0", {"start": v(-60, 38.83) * mm, "end": v(-60, -38.83) * mm});
            skArc(sketch, "E94.0", {"start": v(-54.26, 47.88) * mm, "mid": v(-58.44, 44.2) * mm, "end": v(-60, 38.83) * mm});
            skArc(sketch, "E95.0", {"start": v(54.26, 47.88) * mm, "mid": v(0, 60) * mm, "end": v(-54.26, 47.88) * mm});
            skArc(sketch, "E96.0", {"start": v(60, 38.83) * mm, "mid": v(58.44, 44.2) * mm, "end": v(54.26, 47.88) * mm});
            skLineSegment(sketch, "E97.0", {"start": v(60, 38.83) * mm, "end": v(60, -38.83) * mm});
            skArc(sketch, "E98.0", {"start": v(54.26, -47.88) * mm, "mid": v(58.44, -44.2) * mm, "end": v(60, -38.83) * mm});
            skPoint(sketch, "E99.endSnap0", {"position": v(0, 74.25) * mm});
            skLineSegment(sketch, "E100", {"start": v(-15, 104.25) * mm, "end": v(-15, 92.25) * mm});
            skLineSegment(sketch, "E101", {"start": v(15, 104.25) * mm, "end": v(15, 92.25) * mm});
            skLineSegment(sketch, "E102", {"start": v(15, 92.25) * mm, "end": v(33, 74.25) * mm});
            skLineSegment(sketch, "E103", {"start": v(-15, 92.25) * mm, "end": v(-33, 74.25) * mm});
            skArc(sketch, "E104", {"start": v(15, 104.25) * mm, "mid": v(0, 119.25) * mm, "end": v(-15, 104.25) * mm});
            skLineSegment(sketch, "E105", {"start": v(0, 104.25) * mm, "end": v(0, 74.25) * mm, "construction": true});
            skCircle(sketch, "E106", {"center": v(0, 104.25) * mm, "radius": 6 * mm});
            skLineSegment(sketch, "E107", {"start": v(-74.25, 0) * mm, "end": v(74.25, 0) * mm, "construction": true});
            skLineSegment(sketch, "E108.MirrorCS", {"start": v(-15, -92.25) * mm, "end": v(-33, -74.25) * mm});
            skLineSegment(sketch, "E109.MirrorCS", {"start": v(-15, -104.25) * mm, "end": v(-15, -92.25) * mm});
            skArc(sketch, "E110.MirrorCS", {"start": v(15, -104.25) * mm, "mid": v(0, -119.25) * mm, "end": v(-15, -104.25) * mm});
            skCircle(sketch, "E111.MirrorC", {"center": v(0, -104.25) * mm, "radius": 6 * mm});
            skLineSegment(sketch, "E112.MirrorCS", {"start": v(0, -104.25) * mm, "end": v(0, -74.25) * mm, "construction": true});
            skLineSegment(sketch, "E113.MirrorCS", {"start": v(15, -104.25) * mm, "end": v(15, -92.25) * mm});
            skLineSegment(sketch, "E114.MirrorCS", {"start": v(15, -92.25) * mm, "end": v(33, -74.25) * mm});
            skSolve(sketch);
        }
        {
            var Q0;
            Q0 = qSketchRegion(id + "F16", true);
            var Q1;
            Q1=makeQuery(id+"F2.opExtrude","CAP_FACE",FACE,{"disambiguationData":[OSD([sQuery(id+"F0.wireOp",EDGE,"E12"),sQuery(id+"F0.wireOp",EDGE,"E13"),sQuery(id+"F0.wireOp",EDGE,"E14"),sQuery(id+"F0.wireOp",EDGE,"E15"),sQuery(id+"F0.wireOp",EDGE,"E17.filletArc"),sQuery(id+"F0.wireOp",EDGE,"E18.filletArc"),sQuery(id+"F0.wireOp",EDGE,"E19.filletArc"),sQuery(id+"F0.wireOp",EDGE,"E20.filletArc"),sQuery(id+"F0.wireOp",EDGE,"E25.0"),sQuery(id+"F0.wireOp",EDGE,"E25.1"),sQuery(id+"F0.wireOp",EDGE,"E25.2"),sQuery(id+"F0.wireOp",EDGE,"E25.3"),sQuery(id+"F0.wireOp",EDGE,"E25.4"),sQuery(id+"F0.wireOp",EDGE,"E25.5"),sQuery(id+"F0.wireOp",EDGE,"E25.6"),sQuery(id+"F0.wireOp",EDGE,"E25.7")])],"isStart":false});
            extrude(context, id + "F17", {"entities" : qUnion([Q0]), "endBound" : BoundingType.UP_TO_SURFACE, "depth" : 25 * mm, "endBoundEntityFace" : qUnion([Q1]), "offsetDistance" : 25 * mm});
        }
    });
